# Revit family: Cabinet_Big-Drawer_No-Doors_Moduline
name_source: partatom
category: Furniture
units: mm (PartAtom-declared; Revit-internal decimal feet)

## family parameters
Always vertical = Yes
Classification Number = 23.40.20.00
Cut with Voids When Loaded = No
Enable Cutting in Views = No
Render Appearance Source = Family Geometry
Room Calculation Point = No
Shared = No
Work Plane-Based = No

## types (4) — shared parameters
Depth = 24 "
Drawer Clearance = 20.75 "
Keynote = 12 35 00
Manufacturer = Moduline Aluminum Cabinets
Model = Pro II Big Drawer Units
Product Page URL = https://www.arcat.com
URL = https://modulinecabinets.com
zero-valued in all types: Default Elevation

## per-type parameters (varying)
| type | 32" Height Drawers Configuration | 36" Height Drawers Configuration | Description | Handle Length | Height | Left Drawers Segment Length | Right Drawers Segment Length | Width |
| 32"H x 24"D x 48"W | Yes | No | Modular Big Drawer Unit, 32" Height x 24" Depth x 48" Width | 44.5 " | 31.875 " | 28.5 " | 14 " | 48 " |
| 36"H x 24"D x 60"W | No | Yes | Modular Big Drawer Unit, 36" Height x 24" Depth x 60" Width | 56.5 " | 35.875 " | 32 " | 22.5 " | 60 " |
| 36"H x 24"D x 48"W | No | Yes | Modular Big Drawer Unit, 36" Height x 24" Depth x 48" Width | 44.5 " | 35.875 " | 28.5 " | 14 " | 48 " |
| 32"H x 24"D x 60"W | Yes | No | Modular Big Drawer Unit, 32" Height x 24" Depth x 60" Width | 56.5 " | 31.875 " | 32 " | 22.5 " | 60 " |

## geometry (parser evidence)
native form markers: Sweep x5
no freeform markers — native parametric forms only
